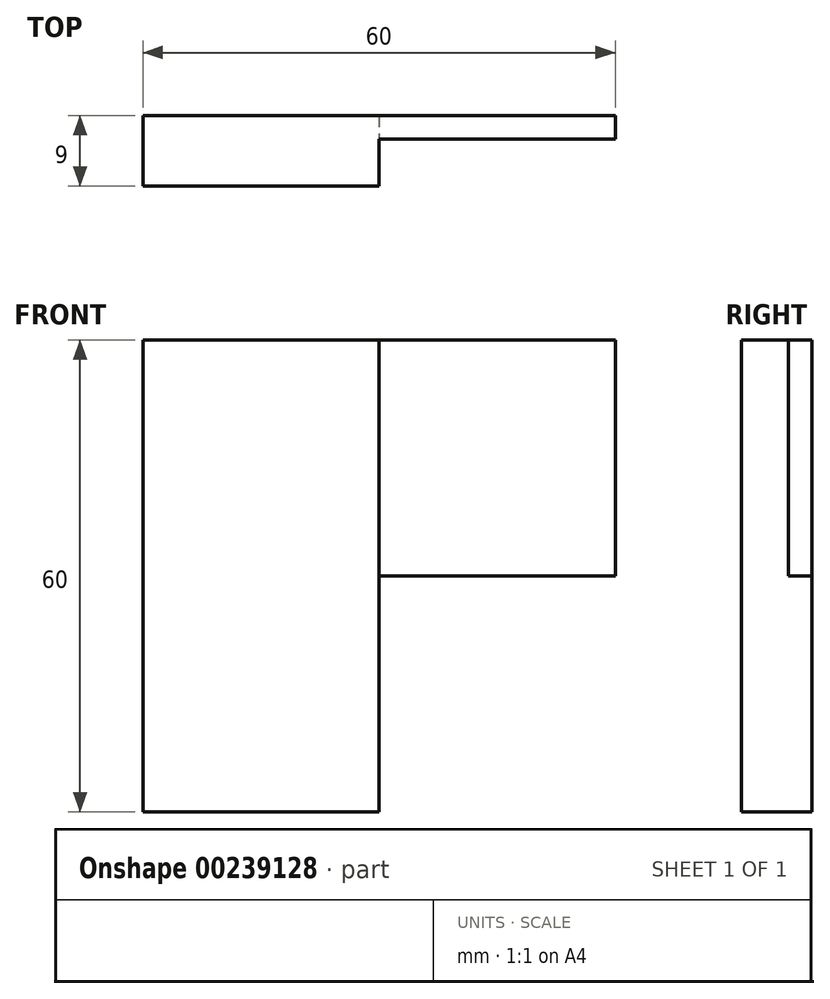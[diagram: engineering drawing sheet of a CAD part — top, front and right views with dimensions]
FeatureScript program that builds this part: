
annotation { "Feature Type Name" : "Feature", "Feature Type Description" : "" }
export const myFeature = defineFeature(function(context is Context, id is Id, definition is map)
    precondition{}
    {
        {
            assignVariable(context, id + "F0", {"name" : "e", "anyValue" : 3});
        }
        {
            var Q0;
            Q0=qCreatedBy(makeId("Front.planeOp"),FACE);
            var sketch = newSketch(context, id + "F1", { "sketchPlane" : qUnion([Q0])});
            skLineSegment(sketch, "E0.bottom", {"start": v(30, 30) * mm, "end": v(-30, 30) * mm});
            skLineSegment(sketch, "E0.top", {"start": v(30, -30) * mm, "end": v(-30, -30) * mm});
            skLineSegment(sketch, "E0.left", {"start": v(30, 30) * mm, "end": v(30, -30) * mm});
            skLineSegment(sketch, "E0.right", {"start": v(-30, 30) * mm, "end": v(-30, -30) * mm});
            skPoint(sketch, "E0.middle", {"position": v(0, 0) * mm});
            skSolve(sketch);
        }
        {
            var Q0;
            Q0 = qSketchRegion(id + "F1", true);
            extrude(context, id + "F2", {"entities" : qUnion([Q0]), "endBound" : BoundingType.SYMMETRIC, "depth" : (3 * getVariable(context, 'e')) * mm});
        }
        {
            var Q0;
            Q0=makeQuery(id+"F2.opExtrude","CAP_FACE",FACE,{"disambiguationData":[OSD([sQuery(id+"F1.wireOp",EDGE,"E0.bottom"),sQuery(id+"F1.wireOp",EDGE,"E0.top"),sQuery(id+"F1.wireOp",EDGE,"E0.left"),sQuery(id+"F1.wireOp",EDGE,"E0.right")])],"isStart":false});
            var sketch = newSketch(context, id + "F3", { "sketchPlane" : qUnion([Q0])});
            skLineSegment(sketch, "E1.bottom", {"start": v(30, 30) * mm, "end": v(0, 30) * mm});
            skLineSegment(sketch, "E1.top", {"start": v(30, 0) * mm, "end": v(0, 0) * mm});
            skLineSegment(sketch, "E1.left", {"start": v(30, 30) * mm, "end": v(30, 0) * mm});
            skLineSegment(sketch, "E1.right", {"start": v(0, 30) * mm, "end": v(0, 0) * mm});
            skSolve(sketch);
        }
        {
            var Q0;
            Q0 = qSketchRegion(id + "F3", true);
            extrude(context, id + "F4", {"entities" : qUnion([Q0]), "operationType" : NewBodyOperationType.REMOVE, "oppositeDirection" : true, "depth" : (2 * getVariable(context, 'e')) * mm});
        }
        {
            var Q0;
            Q0=makeQuery(id+"F2.opExtrude","CAP_FACE",FACE,{"disambiguationData":[OSD([sQuery(id+"F1.wireOp",EDGE,"E0.bottom"),sQuery(id+"F1.wireOp",EDGE,"E0.top"),sQuery(id+"F1.wireOp",EDGE,"E0.left"),sQuery(id+"F1.wireOp",EDGE,"E0.right")])],"isStart":false});
            var sketch = newSketch(context, id + "F5", { "sketchPlane" : qUnion([Q0])});
            skLineSegment(sketch, "E2.bottom", {"start": v(0, 0) * mm, "end": v(30, 0) * mm});
            skLineSegment(sketch, "E2.top", {"start": v(0, -30) * mm, "end": v(30, -30) * mm});
            skLineSegment(sketch, "E2.left", {"start": v(0, 0) * mm, "end": v(0, -30) * mm});
            skLineSegment(sketch, "E2.right", {"start": v(30, 0) * mm, "end": v(30, -30) * mm});
            skSolve(sketch);
        }
        {
            var Q0;
            Q0 = qSketchRegion(id + "F5", true);
            extrude(context, id + "F6", {"entities" : qUnion([Q0]), "operationType" : NewBodyOperationType.REMOVE, "endBound" : BoundingType.THROUGH_ALL, "oppositeDirection" : true, "depth" : 25 * mm});
        }
        {
            var Q0;
            Q0=makeQuery(id+"F2.opExtrude","SWEPT_FACE",FACE,{"disambiguationData":[OSD([sQuery(id+"F1.wireOp",EDGE,"E0.top")])]});
            var sketch = newSketch(context, id + "F7", { "sketchPlane" : qUnion([Q0])});
            skLineSegment(sketch, "E3.bottom", {"start": v(-30, -45) * mm, "end": v(0, -45) * mm});
            skLineSegment(sketch, "E3.top", {"start": v(-30, -15) * mm, "end": v(0, -15) * mm});
            skLineSegment(sketch, "E3.left", {"start": v(-30, -45) * mm, "end": v(-30, -15) * mm});
            skLineSegment(sketch, "E3.right", {"start": v(0, -45) * mm, "end": v(0, -15) * mm});
            skLineSegment(sketch, "E4.bottom", {"start": v(-30, 45) * mm, "end": v(0, 45) * mm});
            skLineSegment(sketch, "E4.top", {"start": v(-30, 15) * mm, "end": v(0, 15) * mm});
            skLineSegment(sketch, "E4.left", {"start": v(-30, 45) * mm, "end": v(-30, 15) * mm});
            skLineSegment(sketch, "E4.right", {"start": v(0, 45) * mm, "end": v(0, 15) * mm});
            skSolve(sketch);
        }
        {
            var Q0;
            Q0 = qSketchRegion(id + "F7", true);
            extrude(context, id + "F8", {"entities" : qUnion([Q0]), "operationType" : NewBodyOperationType.REMOVE, "oppositeDirection" : true, "depth" : (getVariable(context, 'e')) * mm});
        }
    });
